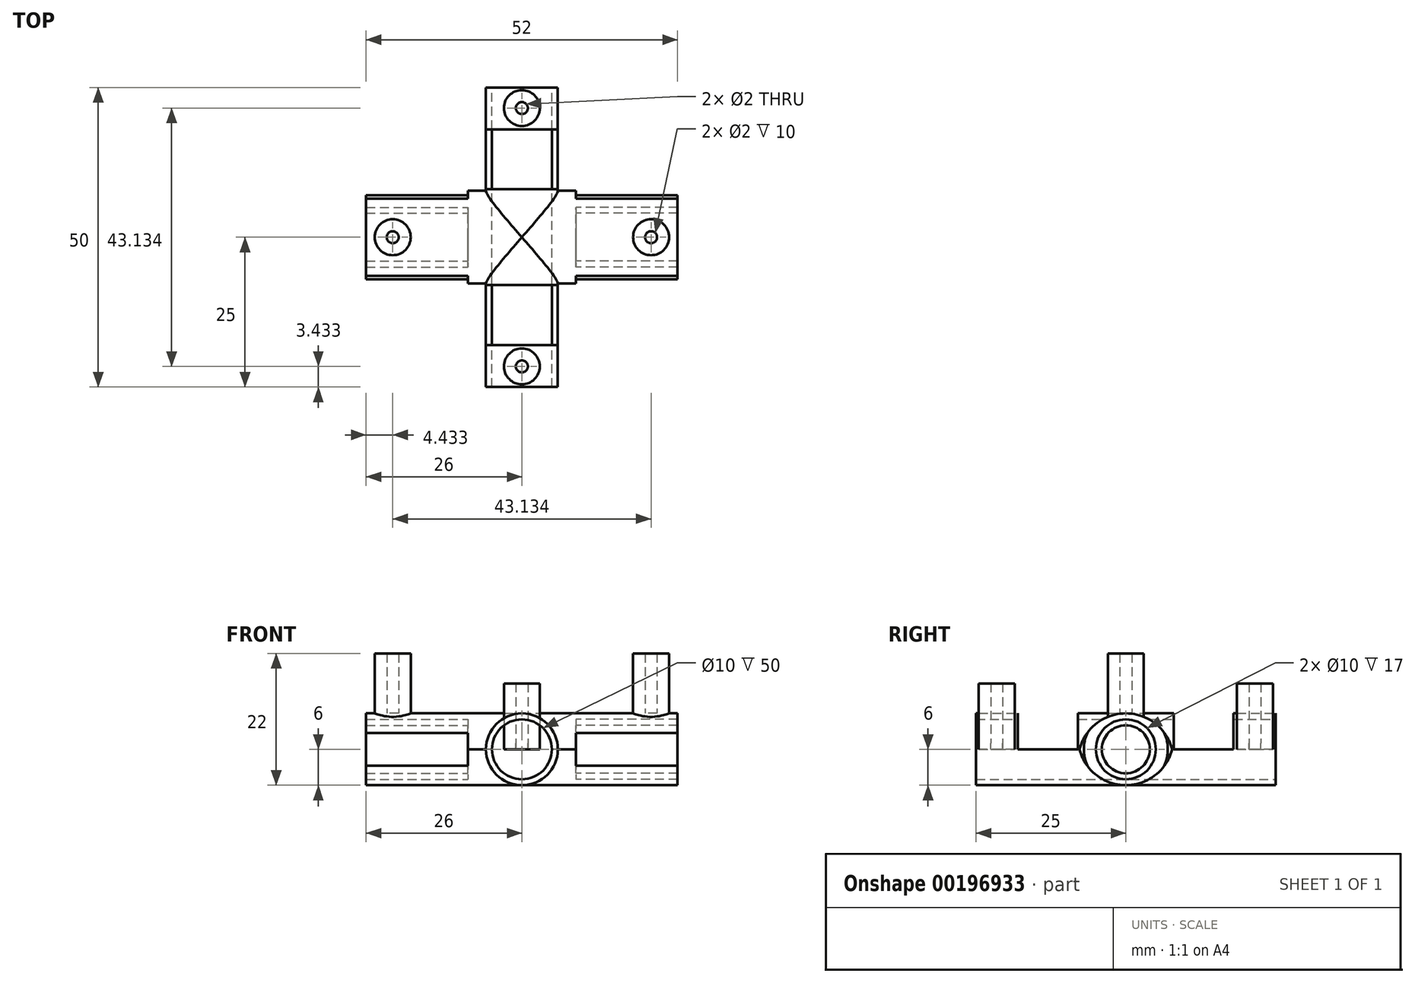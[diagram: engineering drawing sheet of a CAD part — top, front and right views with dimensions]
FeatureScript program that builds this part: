
annotation { "Feature Type Name" : "Feature", "Feature Type Description" : "" }
export const myFeature = defineFeature(function(context is Context, id is Id, definition is map)
    precondition{}
    {
        {
            var Q0;
            Q0=qCreatedBy(makeId("Front.planeOp"),FACE);
            var sketch = newSketch(context, id + "F0", { "sketchPlane" : qUnion([Q0])});
            skCircle(sketch, "E0", {"center": v(0, 0) * mm, "radius": 4 * mm});
            skCircle(sketch, "E1", {"center": v(0, 0) * mm, "radius": 5 * mm});
            skCircle(sketch, "E2", {"center": v(0, 0) * mm, "radius": 6 * mm});
            skLineSegment(sketch, "E3", {"start": v(0, 6) * mm, "end": v(0, 9.66) * mm, "construction": true});
            skLineSegment(sketch, "E4", {"start": v(0, 9.66) * mm, "end": v(2, 9.66) * mm});
            skLineSegment(sketch, "E5", {"start": v(2, 9.66) * mm, "end": v(2, 5.66) * mm});
            skLineSegment(sketch, "E6.MirrorCS", {"start": v(-2, 9.66) * mm, "end": v(-2, 5.66) * mm});
            skLineSegment(sketch, "E7.MirrorCS", {"start": v(0, 9.66) * mm, "end": v(-2, 9.66) * mm});
            skLineSegment(sketch, "E8.bottom", {"start": v(9, 6) * mm, "end": v(-9, 6) * mm});
            skLineSegment(sketch, "E8.top", {"start": v(9, -6) * mm, "end": v(-9, -6) * mm});
            skLineSegment(sketch, "E8.left", {"start": v(9, 6) * mm, "end": v(9, -6) * mm});
            skLineSegment(sketch, "E8.right", {"start": v(-9, 6) * mm, "end": v(-9, -6) * mm});
            skSolve(sketch);
        }
        {
            var Q0;
            Q0=makeQuery(id+"F0.imprint","IMPRINT",FACE,{"disambiguationData":[TD([[makeQuery(id+"F0.imprint","IMPRINT",EDGE,{"derivedFrom":sQuery(id+"F0.wireOp",EDGE,"E1")}),-1.0]])]});
            extrude(context, id + "F1", {"entities" : qUnion([Q0]), "endBound" : BoundingType.SYMMETRIC, "depth" : 50 * mm});
        }
        {
            var Q0;
            {var subQ0=sQuery(id+"F0.wireOp",EDGE,"E8.right");Q0=makeQuery(id+"F0.imprint","IMPRINT",FACE,{"disambiguationData":[TD([[makeQuery(id+"F0.imprint","IMPRINT",EDGE,{"derivedFrom":subQ0}),1.0]])]});}
            var Q1;
            {var subQ0=sQuery(id+"F0.wireOp",EDGE,"E8.left");Q1=makeQuery(id+"F0.imprint","IMPRINT",FACE,{"disambiguationData":[TD([[makeQuery(id+"F0.imprint","IMPRINT",EDGE,{"derivedFrom":subQ0}),-1.0]])]});}
            var Q2;
            {var subQ0=sQuery(id+"F0.wireOp",EDGE,"E6.MirrorCS");var subQ1=sQuery(id+"F0.wireOp",EDGE,"E2");var subQ2=makeQuery(id+"F0.imprint","INTERSECT",VERTEX,{"derivedFrom":[subQ1,subQ0]});Q2=makeQuery(id+"F0.imprint","IMPRINT",FACE,{"disambiguationData":[TD([[makeQuery(id+"F0.imprint","IMPRINT",EDGE,{"disambiguationData":[TD([[subQ2,1.0]])],"derivedFrom":subQ1}),-1.0]])]});}
            var Q3;
            {var subQ0=sQuery(id+"F0.wireOp",EDGE,"E5");var subQ1=sQuery(id+"F0.wireOp",EDGE,"E2");var subQ2=makeQuery(id+"F0.imprint","INTERSECT",VERTEX,{"derivedFrom":[subQ1,subQ0]});Q3=makeQuery(id+"F0.imprint","IMPRINT",FACE,{"disambiguationData":[TD([[makeQuery(id+"F0.imprint","IMPRINT",EDGE,{"disambiguationData":[TD([[subQ2,-1.0]])],"derivedFrom":subQ1}),-1.0]])]});}
            extrude(context, id + "F2", {"entities" : qUnion([Q0, Q1, Q2, Q3]), "operationType" : NewBodyOperationType.ADD, "endBound" : BoundingType.SYMMETRIC, "depth" : 16 * mm});
        }
        {
            var Q0;
            Q0=makeQuery(id+"F2.opExtrude","SWEPT_FACE",FACE,{"disambiguationData":[OSD([sQuery(id+"F0.wireOp",EDGE,"E8.right")])]});
            var sketch = newSketch(context, id + "F3", { "sketchPlane" : qUnion([Q0])});
            skCircle(sketch, "E9", {"center": v(0, 0) * mm, "radius": 4 * mm});
            skCircle(sketch, "E10", {"center": v(0, 0) * mm, "radius": 5 * mm});
            skCircle(sketch, "E11", {"center": v(0, 0) * mm, "radius": 7 * mm});
            skLineSegment(sketch, "E12.bottom", {"start": v(-18, 10.77) * mm, "end": v(-8, 10.77) * mm});
            skLineSegment(sketch, "E12.top", {"start": v(-18, 0) * mm, "end": v(-8, 0) * mm});
            skLineSegment(sketch, "E12.left", {"start": v(-18, 10.77) * mm, "end": v(-18, 0) * mm});
            skLineSegment(sketch, "E12.right", {"start": v(-8, 10.77) * mm, "end": v(-8, 0) * mm});
            skPoint(sketch, "E12.middle", {"position": v(-13, 5.38) * mm});
            skLineSegment(sketch, "E13", {"start": v(0, -9.3) * mm, "end": v(0, 16.63) * mm, "construction": true});
            skLineSegment(sketch, "E14.MirrorCS", {"start": v(8, 10.77) * mm, "end": v(8, 0) * mm});
            skLineSegment(sketch, "E15.MirrorCS", {"start": v(18, 0) * mm, "end": v(8, 0) * mm});
            skLineSegment(sketch, "E16.MirrorCS", {"start": v(18, 10.77) * mm, "end": v(18, 0) * mm});
            skLineSegment(sketch, "E17.MirrorCS", {"start": v(18, 10.77) * mm, "end": v(8, 10.77) * mm});
            skSolve(sketch);
        }
        {
            var Q0;
            Q0=makeQuery(id+"F3.imprint","IMPRINT",FACE,{"disambiguationData":[TD([[makeQuery(id+"F3.imprint","IMPRINT",EDGE,{"derivedFrom":sQuery(id+"F3.wireOp",EDGE,"E10")}),-1.0]])]});
            extrude(context, id + "F4", {"entities" : qUnion([Q0]), "operationType" : NewBodyOperationType.ADD, "depth" : 17 * mm});
        }
        {
            var Q0;
            Q0=makeQuery(id+"F3.imprint","IMPRINT",FACE,{"disambiguationData":[TD([[makeQuery(id+"F3.imprint","IMPRINT",EDGE,{"derivedFrom":sQuery(id+"F3.wireOp",EDGE,"E9")}),1.0]])]});
            var Q1;
            Q1=makeQuery(id+"F4.opExtrude","CAP_FACE",FACE,{"disambiguationData":[OSD([sQuery(id+"F3.wireOp",EDGE,"E10"),sQuery(id+"F3.wireOp",EDGE,"E11")])],"isStart":false});
            extrude(context, id + "F5", {"entities" : qUnion([Q0]), "operationType" : NewBodyOperationType.ADD, "endBound" : BoundingType.UP_TO_SURFACE, "endBoundEntityFace" : qUnion([Q1]), "depth" : 8 * mm});
        }
        {
            var Q0;
            Q0=makeQuery(id+"F1.opExtrude","SWEPT_BODY",BODY,{"disambiguationData":[OSD([sQuery(id+"F0.wireOp",EDGE,"E1"),sQuery(id+"F0.wireOp",EDGE,"E2")])]});
            var Q1;
            Q1=qCreatedBy(makeId("Right.planeOp"),FACE);
            mirror(context, id + "F6", {"operationType" : NewBodyOperationType.ADD, "entities" : qUnion([Q0]), "mirrorPlane" : qUnion([Q1])});
        }
        {
            var Q0;
            {var subQ0=sQuery(id+"F0.wireOp",EDGE,"E8.bottom");var subQ1=makeQuery(id+"F0.imprint","INTERSECT",VERTEX,{"derivedFrom":[sQuery(id+"F0.wireOp",EDGE,"E6.MirrorCS"),subQ0]});var subQ3=makeQuery(id+"F0.imprint","INTERSECT",VERTEX,{"derivedFrom":[sQuery(id+"F0.wireOp",EDGE,"E5"),subQ0]});Q0=makeQuery(id+"F2.boolean.opBoolean","MERGE",FACE,{"derivedFrom":[makeQuery(id+"F2.opExtrude","SWEPT_FACE",FACE,{"disambiguationData":[OSD([subQ0]),TDD([makeQuery(id+"F0.imprint","IMPRINT",EDGE,{"disambiguationData":[TD([[makeQuery(id+"F0.imprint","INTERSECT",VERTEX,{"derivedFrom":[subQ0,sQuery(id+"F0.wireOp",EDGE,"E8.left")]}),-1.0]])],"derivedFrom":subQ0}),makeQuery(id+"F0.imprint","IMPRINT",EDGE,{"disambiguationData":[TD([[subQ3,-1.0]])],"derivedFrom":subQ0})])]}),makeQuery(id+"F2.opExtrude","SWEPT_FACE",FACE,{"disambiguationData":[OSD([subQ0]),TDD([makeQuery(id+"F0.imprint","IMPRINT",EDGE,{"disambiguationData":[TD([[subQ1,1.0]])],"derivedFrom":subQ0}),makeQuery(id+"F0.imprint","IMPRINT",EDGE,{"disambiguationData":[TD([[makeQuery(id+"F0.imprint","INTERSECT",VERTEX,{"derivedFrom":[subQ0,sQuery(id+"F0.wireOp",EDGE,"E8.right")]}),1.0]])],"derivedFrom":subQ0})])]})]});}
            var sketch = newSketch(context, id + "F7", { "sketchPlane" : qUnion([Q0])});
            skLineSegment(sketch, "E18", {"start": v(-21.57, 0) * mm, "end": v(0, 21.57) * mm, "construction": true});
            skLineSegment(sketch, "E19", {"start": v(0, 21.57) * mm, "end": v(21.57, 0) * mm, "construction": true});
            skLineSegment(sketch, "E20", {"start": v(21.57, 0) * mm, "end": v(0, -21.57) * mm, "construction": true});
            skLineSegment(sketch, "E21", {"start": v(0, -21.57) * mm, "end": v(-21.57, 0) * mm, "construction": true});
            skLineSegment(sketch, "E22", {"start": v(0, 21.57) * mm, "end": v(0, -21.57) * mm, "construction": true});
            skLineSegment(sketch, "E23", {"start": v(-21.57, 0) * mm, "end": v(21.57, 0) * mm, "construction": true});
            skLineSegment(sketch, "E24", {"start": v(-11, 0) * mm, "end": v(11, 0) * mm, "construction": true});
            skLineSegment(sketch, "E25", {"start": v(0, 8) * mm, "end": v(0, -8) * mm, "construction": true});
            skCircle(sketch, "E26", {"center": v(0, 21.57) * mm, "radius": 1 * mm});
            skCircle(sketch, "E27", {"center": v(21.57, 0) * mm, "radius": 1 * mm});
            skCircle(sketch, "E28", {"center": v(0, -21.57) * mm, "radius": 1 * mm});
            skCircle(sketch, "E29", {"center": v(-21.57, 0) * mm, "radius": 1 * mm});
            skCircle(sketch, "E30.0", {"center": v(0, -21.57) * mm, "radius": 3 * mm});
            skCircle(sketch, "E31", {"center": v(21.57, 0) * mm, "radius": 3 * mm});
            skCircle(sketch, "E32", {"center": v(0, 21.57) * mm, "radius": 3 * mm});
            skCircle(sketch, "E33", {"center": v(0, 21.57) * mm, "radius": 2 * mm});
            skCircle(sketch, "E34", {"center": v(-21.57, 0) * mm, "radius": 3 * mm});
            skCircle(sketch, "E35", {"center": v(-21.57, 0) * mm, "radius": 2 * mm});
            skCircle(sketch, "E36", {"center": v(0, -21.57) * mm, "radius": 2 * mm});
            skCircle(sketch, "E37", {"center": v(21.57, 0) * mm, "radius": 2 * mm});
            skSolve(sketch);
        }
        {
            var Q0;
            Q0=makeQuery(id+"F7.imprint","IMPRINT",FACE,{"disambiguationData":[TD([[makeQuery(id+"F7.imprint","IMPRINT",EDGE,{"derivedFrom":sQuery(id+"F7.wireOp",EDGE,"E30.0")}),1.0]])]});
            var Q1;
            Q1=makeQuery(id+"F7.imprint","IMPRINT",FACE,{"disambiguationData":[TD([[makeQuery(id+"F7.imprint","IMPRINT",EDGE,{"derivedFrom":sQuery(id+"F7.wireOp",EDGE,"E28")}),-1.0]])]});
            var Q2;
            Q2=makeQuery(id+"F7.imprint","IMPRINT",FACE,{"disambiguationData":[TD([[makeQuery(id+"F7.imprint","IMPRINT",EDGE,{"derivedFrom":sQuery(id+"F7.wireOp",EDGE,"E27")}),-1.0]])]});
            var Q3;
            Q3=makeQuery(id+"F7.imprint","IMPRINT",FACE,{"disambiguationData":[TD([[makeQuery(id+"F7.imprint","IMPRINT",EDGE,{"derivedFrom":sQuery(id+"F7.wireOp",EDGE,"E31")}),1.0]])]});
            var Q4;
            Q4=makeQuery(id+"F7.imprint","IMPRINT",FACE,{"disambiguationData":[TD([[makeQuery(id+"F7.imprint","IMPRINT",EDGE,{"derivedFrom":sQuery(id+"F7.wireOp",EDGE,"E26")}),-1.0]])]});
            var Q5;
            Q5=makeQuery(id+"F7.imprint","IMPRINT",FACE,{"disambiguationData":[TD([[makeQuery(id+"F7.imprint","IMPRINT",EDGE,{"derivedFrom":sQuery(id+"F7.wireOp",EDGE,"E32")}),1.0]])]});
            var Q6;
            Q6=makeQuery(id+"F7.imprint","IMPRINT",FACE,{"disambiguationData":[TD([[makeQuery(id+"F7.imprint","IMPRINT",EDGE,{"derivedFrom":sQuery(id+"F7.wireOp",EDGE,"E29")}),-1.0]])]});
            var Q7;
            Q7=makeQuery(id+"F7.imprint","IMPRINT",FACE,{"disambiguationData":[TD([[makeQuery(id+"F7.imprint","IMPRINT",EDGE,{"derivedFrom":sQuery(id+"F7.wireOp",EDGE,"E34")}),1.0]])]});
            extrude(context, id + "F11", {"entities" : qUnion([Q0, Q1, Q2, Q3, Q4, Q5, Q6, Q7]), "operationType" : NewBodyOperationType.ADD, "depth" : 10 * mm});
        }
        {
            var Q0;
            {var subQ0=sQuery(id+"F0.wireOp",EDGE,"E8.bottom");var subQ1=makeQuery(id+"F0.imprint","INTERSECT",VERTEX,{"derivedFrom":[sQuery(id+"F0.wireOp",EDGE,"E5"),subQ0]});Q0=makeQuery(id+"F2.opExtrude","CAP_EDGE",EDGE,{"disambiguationData":[OSD([subQ0]),TDD([makeQuery(id+"F0.imprint","IMPRINT",EDGE,{"disambiguationData":[TD([[makeQuery(id+"F0.imprint","INTERSECT",VERTEX,{"derivedFrom":[subQ0,sQuery(id+"F0.wireOp",EDGE,"E8.left")]}),-1.0]])],"derivedFrom":subQ0}),makeQuery(id+"F0.imprint","IMPRINT",EDGE,{"disambiguationData":[TD([[subQ1,-1.0]])],"derivedFrom":subQ0})])],"isStart":false});}
            var Q1;
            {var subQ0=sQuery(id+"F0.wireOp",EDGE,"E8.bottom");var subQ1=makeQuery(id+"F0.imprint","INTERSECT",VERTEX,{"derivedFrom":[sQuery(id+"F0.wireOp",EDGE,"E6.MirrorCS"),subQ0]});Q1=makeQuery(id+"F2.opExtrude","CAP_EDGE",EDGE,{"disambiguationData":[OSD([subQ0]),TDD([makeQuery(id+"F0.imprint","IMPRINT",EDGE,{"disambiguationData":[TD([[subQ1,1.0]])],"derivedFrom":subQ0}),makeQuery(id+"F0.imprint","IMPRINT",EDGE,{"disambiguationData":[TD([[makeQuery(id+"F0.imprint","INTERSECT",VERTEX,{"derivedFrom":[subQ0,sQuery(id+"F0.wireOp",EDGE,"E8.right")]}),1.0]])],"derivedFrom":subQ0})])],"isStart":false});}
            var Q2;
            {var subQ0=sQuery(id+"F0.wireOp",EDGE,"E8.top");Q2=makeQuery(id+"F2.opExtrude","CAP_EDGE",EDGE,{"disambiguationData":[OSD([subQ0]),TDD([makeQuery(id+"F0.imprint","IMPRINT",EDGE,{"disambiguationData":[TD([[makeQuery(id+"F0.imprint","INTERSECT",VERTEX,{"derivedFrom":[subQ0,sQuery(id+"F0.wireOp",EDGE,"E8.left")]}),-1.0]])],"derivedFrom":subQ0})])],"isStart":false});}
            var Q3;
            {var subQ0=sQuery(id+"F0.wireOp",EDGE,"E8.top");Q3=makeQuery(id+"F2.opExtrude","CAP_EDGE",EDGE,{"disambiguationData":[OSD([subQ0]),TDD([makeQuery(id+"F0.imprint","IMPRINT",EDGE,{"disambiguationData":[TD([[makeQuery(id+"F0.imprint","INTERSECT",VERTEX,{"derivedFrom":[subQ0,sQuery(id+"F0.wireOp",EDGE,"E8.right")]}),1.0]])],"derivedFrom":subQ0})])],"isStart":true});}
            var Q4;
            {var subQ0=sQuery(id+"F0.wireOp",EDGE,"E8.bottom");var subQ1=makeQuery(id+"F0.imprint","INTERSECT",VERTEX,{"derivedFrom":[sQuery(id+"F0.wireOp",EDGE,"E5"),subQ0]});Q4=makeQuery(id+"F2.opExtrude","CAP_EDGE",EDGE,{"disambiguationData":[OSD([subQ0]),TDD([makeQuery(id+"F0.imprint","IMPRINT",EDGE,{"disambiguationData":[TD([[makeQuery(id+"F0.imprint","INTERSECT",VERTEX,{"derivedFrom":[subQ0,sQuery(id+"F0.wireOp",EDGE,"E8.left")]}),-1.0]])],"derivedFrom":subQ0}),makeQuery(id+"F0.imprint","IMPRINT",EDGE,{"disambiguationData":[TD([[subQ1,-1.0]])],"derivedFrom":subQ0})])],"isStart":true});}
            fillet(context, id + "F8", {"entities" : qUnion([Q0, Q1, Q2, Q3, Q4]), "radius" : 8 * mm, "tangentPropagation" : true, "allowEdgeOverflow" : false});
        }
        {
            var Q0;
            {var subQ0=sQuery(id+"F3.wireOp",EDGE,"E15.MirrorCS");Q0=makeQuery(id+"F3.imprint","IMPRINT",FACE,{"disambiguationData":[TD([[makeQuery(id+"F3.imprint","IMPRINT",EDGE,{"derivedFrom":subQ0}),-1.0]])]});}
            var Q1;
            {var subQ4=sQuery(id+"F3.wireOp",EDGE,"E12.bottom");Q1=makeQuery(id+"F3.imprint","IMPRINT",FACE,{"disambiguationData":[TD([[makeQuery(id+"F3.imprint","IMPRINT",EDGE,{"derivedFrom":subQ4}),-1.0]])]});}
            extrude(context, id + "F12", {"entities" : qUnion([Q0, Q1]), "operationType" : NewBodyOperationType.REMOVE, "oppositeDirection" : true, "depth" : 25 * mm});
        }
        {
            var Q0;
            Q0=makeQuery(id+"F1.opExtrude","SWEPT_BODY",BODY,{"disambiguationData":[OSD([sQuery(id+"F0.wireOp",EDGE,"E1"),sQuery(id+"F0.wireOp",EDGE,"E2")])]});
            transform(context, id + "F9", {"entities" : qUnion([Q0]), "transformType" : TransformType.TRANSLATION_3D, "dx" : 0 * mm, "dy" : 0 * mm, "dz" : 5 * mm, "makeCopy" : false});
        }
        {
            var Q0;
            Q0=makeQuery(id+"F11.opExtrude","CAP_FACE",FACE,{"disambiguationData":[OSD([sQuery(id+"F7.wireOp",EDGE,"E26"),sQuery(id+"F7.wireOp",EDGE,"E32")])],"isStart":true});
            var Q1;
            Q1=makeQuery(id+"F11.opExtrude","CAP_FACE",FACE,{"disambiguationData":[OSD([sQuery(id+"F7.wireOp",EDGE,"E28"),sQuery(id+"F7.wireOp",EDGE,"E30.0")])],"isStart":true});
            extrude(context, id + "F10", {"entities" : qUnion([Q0, Q1]), "operationType" : NewBodyOperationType.ADD, "depth" : 1 * mm});
        }
    });
